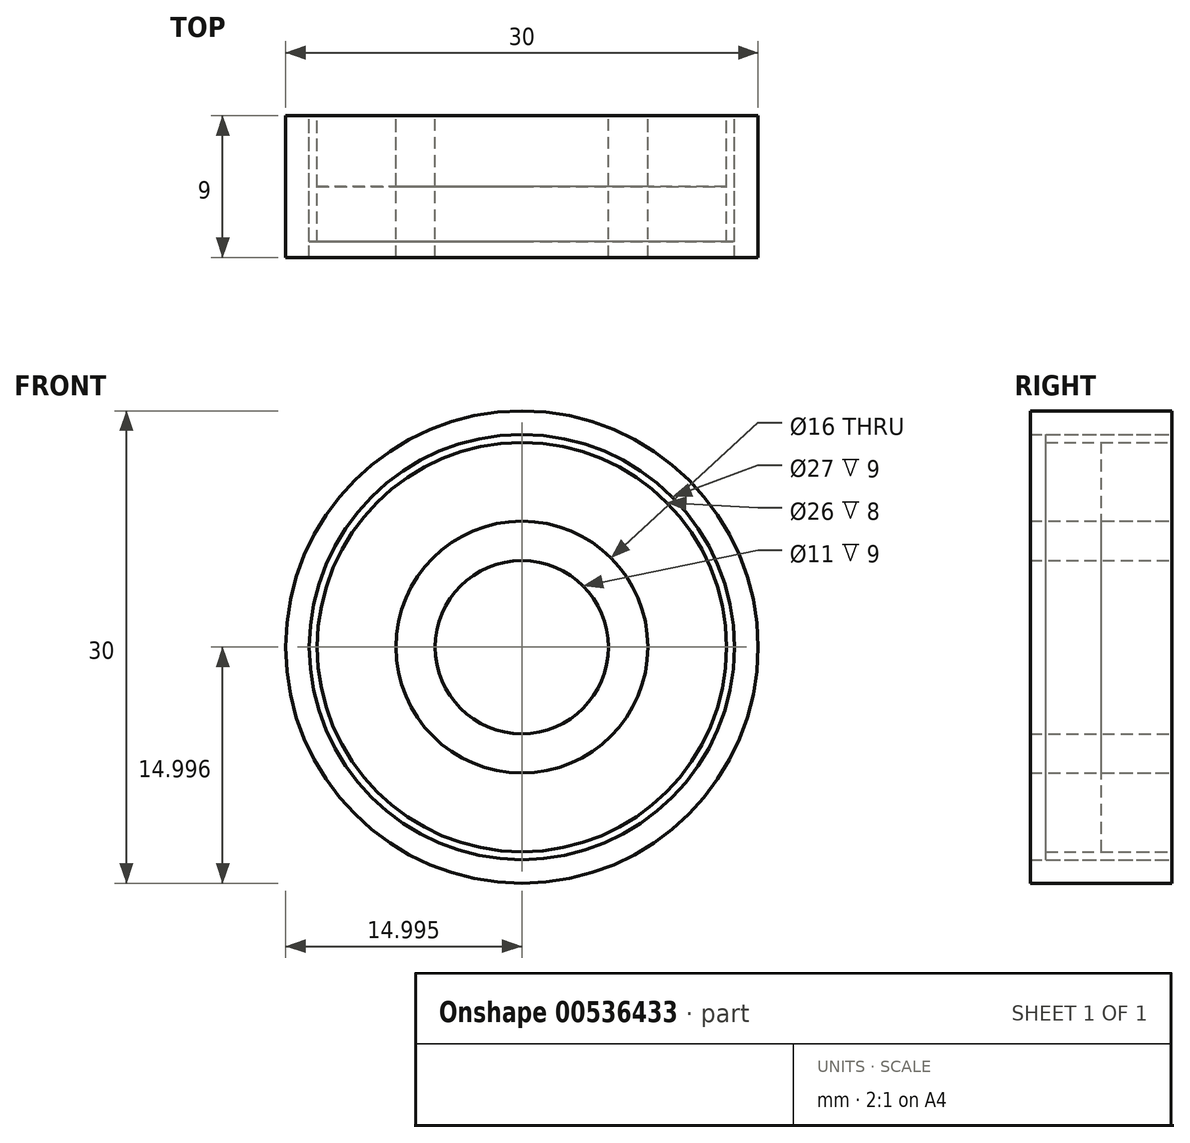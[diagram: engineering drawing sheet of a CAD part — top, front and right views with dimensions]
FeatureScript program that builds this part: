
annotation { "Feature Type Name" : "Feature", "Feature Type Description" : "" }
export const myFeature = defineFeature(function(context is Context, id is Id, definition is map)
    precondition{}
    {
        {
            var Q0;
            Q0=qCreatedBy(makeId("Front.planeOp"),FACE);
            var sketch = newSketch(context, id + "F0", { "sketchPlane" : qUnion([Q0])});
            skCircle(sketch, "E0", {"center": v(-33.97, -3.54) * mm, "radius": 5.5 * mm});
            skCircle(sketch, "E1", {"center": v(-33.97, -3.54) * mm, "radius": 15 * mm});
            skCircle(sketch, "E2", {"center": v(-33.97, -3.54) * mm, "radius": 13.5 * mm});
            skCircle(sketch, "E3", {"center": v(-33.97, -3.54) * mm, "radius": 13 * mm});
            skCircle(sketch, "E4", {"center": v(-33.97, -3.54) * mm, "radius": 8 * mm});
            skSolve(sketch);
        }
        {
            var Q0;
            Q0=makeQuery(id+"F0.imprint","IMPRINT",FACE,{"disambiguationData":[TD([[makeQuery(id+"F0.imprint","IMPRINT",EDGE,{"derivedFrom":sQuery(id+"F0.wireOp",EDGE,"E0")}),-1.0]])]});
            extrude(context, id + "F1", {"entities" : qUnion([Q0]), "depth" : 9 * mm, "offsetDistance" : 25 * mm});
        }
        {
            var Q0;
            Q0=makeQuery(id+"F0.imprint","IMPRINT",FACE,{"disambiguationData":[TD([[makeQuery(id+"F0.imprint","IMPRINT",EDGE,{"derivedFrom":sQuery(id+"F0.wireOp",EDGE,"E1")}),1.0]])]});
            extrude(context, id + "F2", {"entities" : qUnion([Q0]), "depth" : 9 * mm, "offsetDistance" : 25 * mm});
        }
        {
            var Q0;
            Q0=makeQuery(id+"F0.imprint","IMPRINT",FACE,{"disambiguationData":[TD([[makeQuery(id+"F0.imprint","IMPRINT",EDGE,{"derivedFrom":sQuery(id+"F0.wireOp",EDGE,"E2")}),1.0]])]});
            extrude(context, id + "F3", {"entities" : qUnion([Q0]), "depth" : 8 * mm, "offsetDistance" : 25 * mm});
        }
        {
            var Q0;
            Q0=makeQuery(id+"F0.imprint","IMPRINT",FACE,{"disambiguationData":[TD([[makeQuery(id+"F0.imprint","IMPRINT",EDGE,{"derivedFrom":sQuery(id+"F0.wireOp",EDGE,"E3")}),1.0]])]});
            extrude(context, id + "F4", {"entities" : qUnion([Q0]), "depth" : 4.5 * mm, "offsetDistance" : 25 * mm});
        }
    });
